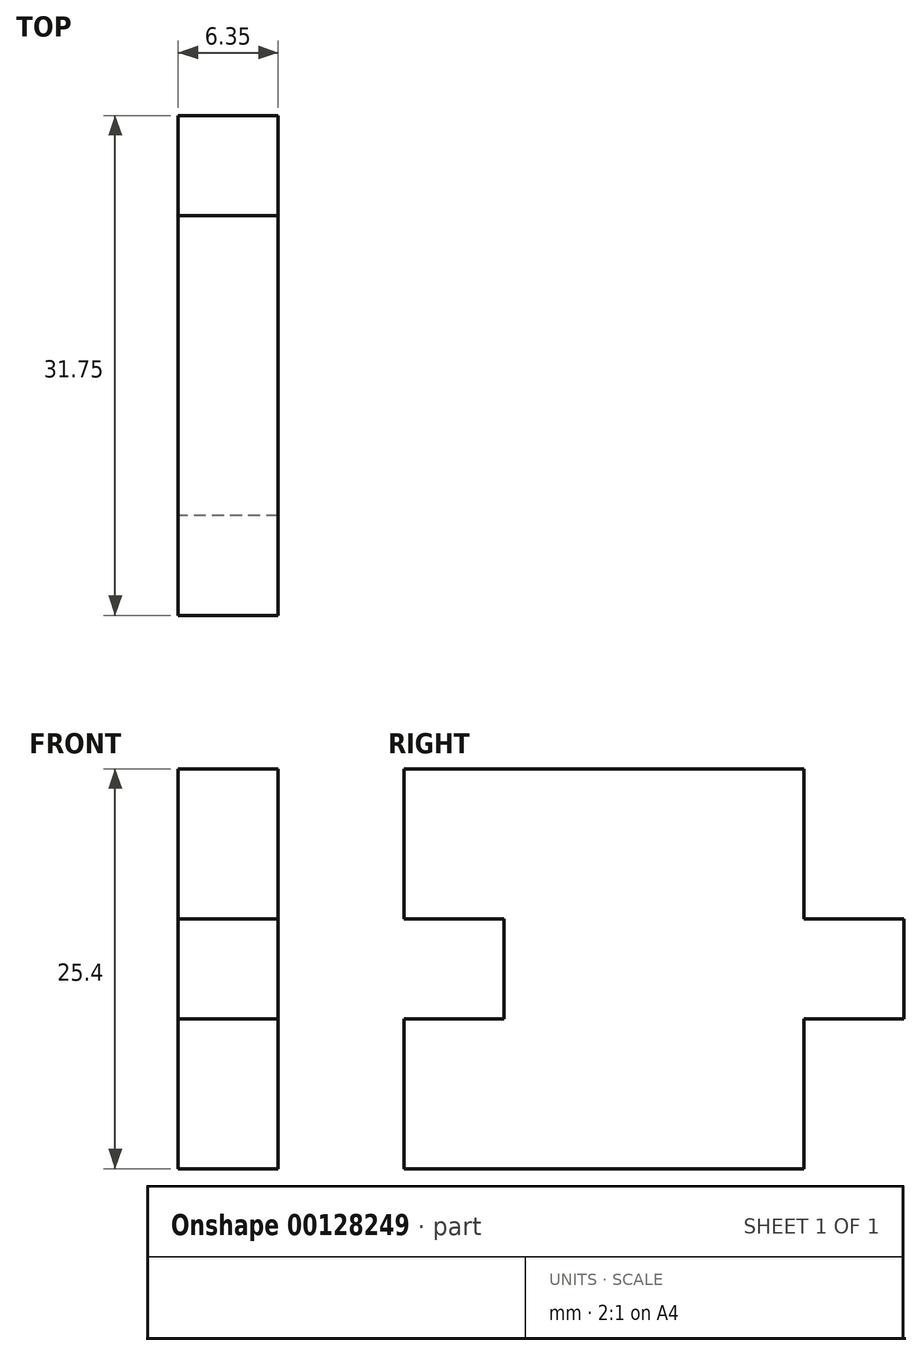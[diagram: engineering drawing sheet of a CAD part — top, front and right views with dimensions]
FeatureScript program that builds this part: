
annotation { "Feature Type Name" : "Feature", "Feature Type Description" : "" }
export const myFeature = defineFeature(function(context is Context, id is Id, definition is map)
    precondition{}
    {
        {
            var Q0;
            Q0=qCreatedBy(makeId("Right.planeOp"),FACE);
            var sketch = newSketch(context, id + "F0", { "sketchPlane" : qUnion([Q0])});
            skLineSegment(sketch, "E0.bottom", {"start": v(0, 0) * mm, "end": v(25.4, 0) * mm});
            skLineSegment(sketch, "E0.top", {"start": v(0, -25.4) * mm, "end": v(25.4, -25.4) * mm});
            skLineSegment(sketch, "E0.left", {"start": v(0, 0) * mm, "end": v(0, -25.4) * mm});
            skLineSegment(sketch, "E0.right", {"start": v(25.4, 0) * mm, "end": v(25.4, -25.4) * mm});
            skLineSegment(sketch, "E1.bottom", {"start": v(0.95, 0) * mm, "end": v(8.9, 0) * mm});
            skLineSegment(sketch, "E1.top", {"start": v(0.95, -6.35) * mm, "end": v(8.9, -6.35) * mm});
            skLineSegment(sketch, "E1.left", {"start": v(0.95, 0) * mm, "end": v(0.95, -6.35) * mm});
            skLineSegment(sketch, "E1.right", {"start": v(8.9, 0) * mm, "end": v(8.9, -6.35) * mm});
            skLineSegment(sketch, "E2.bottom", {"start": v(24.45, 0) * mm, "end": v(16.51, 0) * mm});
            skLineSegment(sketch, "E2.top", {"start": v(24.45, -6.35) * mm, "end": v(16.51, -6.35) * mm});
            skLineSegment(sketch, "E2.left", {"start": v(24.45, 0) * mm, "end": v(24.45, -6.35) * mm});
            skLineSegment(sketch, "E2.right", {"start": v(16.51, 0) * mm, "end": v(16.51, -6.35) * mm});
            skLineSegment(sketch, "E3.bottom", {"start": v(0, -15.88) * mm, "end": v(6.35, -15.88) * mm});
            skLineSegment(sketch, "E3.top", {"start": v(0, -9.53) * mm, "end": v(6.35, -9.53) * mm});
            skLineSegment(sketch, "E3.left", {"start": v(0, -15.88) * mm, "end": v(0, -9.53) * mm});
            skLineSegment(sketch, "E3.right", {"start": v(6.35, -15.88) * mm, "end": v(6.35, -9.53) * mm});
            skLineSegment(sketch, "E4.bottom", {"start": v(9.52, -25.4) * mm, "end": v(15.88, -25.4) * mm});
            skLineSegment(sketch, "E4.top", {"start": v(9.52, -19.05) * mm, "end": v(15.88, -19.05) * mm});
            skLineSegment(sketch, "E4.left", {"start": v(9.52, -25.4) * mm, "end": v(9.52, -19.05) * mm});
            skLineSegment(sketch, "E4.right", {"start": v(15.88, -25.4) * mm, "end": v(15.88, -19.05) * mm});
            skLineSegment(sketch, "E5.bottom", {"start": v(25.4, -9.52) * mm, "end": v(31.75, -9.52) * mm});
            skLineSegment(sketch, "E5.top", {"start": v(25.4, -15.88) * mm, "end": v(31.75, -15.88) * mm});
            skLineSegment(sketch, "E5.left", {"start": v(25.4, -9.52) * mm, "end": v(25.4, -15.88) * mm});
            skLineSegment(sketch, "E5.right", {"start": v(31.75, -9.52) * mm, "end": v(31.75, -15.88) * mm});
            skSolve(sketch);
        }
        {
            var Q0;
            Q0 = qSketchRegion(id + "F0", true);
            extrude(context, id + "F1", {"entities" : qUnion([Q0]), "depth" : 6.35 * mm});
        }
        {
            var Q0;
            Q0=makeQuery(id+"F0.imprint","IMPRINT",FACE,{"disambiguationData":[TD([[makeQuery(id+"F0.imprint","IMPRINT",EDGE,{"derivedFrom":sQuery(id+"F0.wireOp",EDGE,"E1.bottom")}),-1.0]])]});
            var Q1;
            Q1=makeQuery(id+"F0.imprint","IMPRINT",FACE,{"disambiguationData":[TD([[makeQuery(id+"F0.imprint","IMPRINT",EDGE,{"derivedFrom":sQuery(id+"F0.wireOp",EDGE,"E2.bottom")}),1.0]])]});
            var Q2;
            Q2=makeQuery(id+"F0.imprint","IMPRINT",FACE,{"disambiguationData":[TD([[makeQuery(id+"F0.imprint","IMPRINT",EDGE,{"derivedFrom":sQuery(id+"F0.wireOp",EDGE,"E4.bottom")}),1.0]])]});
            var Q3;
            Q3=makeQuery(id+"F0.imprint","IMPRINT",FACE,{"disambiguationData":[TD([[makeQuery(id+"F0.imprint","IMPRINT",EDGE,{"derivedFrom":sQuery(id+"F0.wireOp",EDGE,"E3.bottom")}),1.0]])]});
            extrude(context, id + "F2", {"entities" : qUnion([Q0, Q1, Q2, Q3]), "operationType" : NewBodyOperationType.REMOVE, "depth" : 25.4 * mm});
        }
    });
